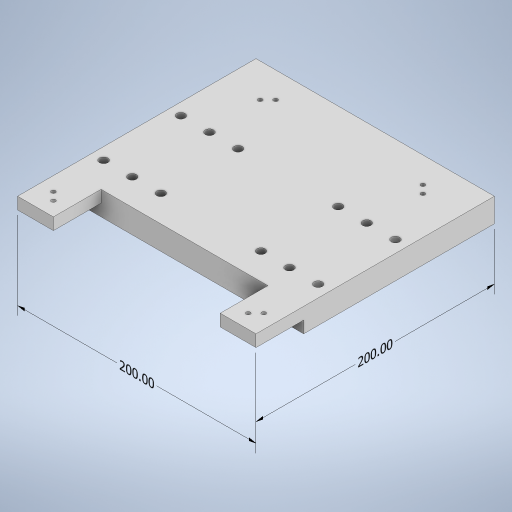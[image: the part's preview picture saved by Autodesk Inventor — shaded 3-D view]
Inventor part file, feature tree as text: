
AUTODESK INVENTOR PART (.ipt)
format: ipt  version: 2023 (Build 270158000, 158)  size: 317,952 bytes
history: native  units: mm
features: sketch x5, other x4, extrude x4, hole x1
ambient origin geometry x8: Origin, YZ Plane, XZ Plane, XY Plane, X Axis, Y Axis, Z Axis, Center Point
bodies: Body1 (feature_tree)
feature tree (14):
  other  "Sólido1"
  other  "Anotaciones"
  extrude  "Extrusión1"  Depth=160.0mm
  extrude  "Extrusión2"  TaperAngle=0.0deg  [1 undecoded]
  extrude  "Extrusión3"  Depth=20.0mm TaperAngle=0.0deg
  extrude  "Extrusión4"  Depth=10.0mm
  hole  "Agujero1"  [1 undecoded]
  sketch  "Boceto1"  dims[d0=200.0mm d1=160.0mm]
  sketch  "Boceto2"  dims[d2=20.0mm d3=0.0mm]
  sketch  "Boceto3"  dims[d4=7.0mm d5=68.0mm d6=80.0mm d7=7.6mm d8=10.0mm d9=7.0mm d10=24.0mm d11=10.0mm d16=0.0mm]
  sketch  "Boceto4"  dims[d19=40.0mm d20=20.0mm d21=0.0mm]
  sketch  "Boceto5"  dims[d22=30.0mm d23=10.0mm d24=40.0mm d25=0.0mm d26=1.75mm d27=8.25mm d28=20.0mm d29=10.0mm d30=10.0mm d31=1.75mm d32=1.75mm d33=1.75mm d34=40.0mm d35=0.0mm d36=11.749873mm d37=40.0mm d38=29.999873mm d39=21.75mm d40=11.75mm d41=28.300341mm d42=11.749873mm d43=0.0mm d44=0.0mm d45=3.5mm d46=6.0mm d47=4.0mm d48=2.0mm d49=90.0deg d50=8.0mm d51=20.594885mm d58=30.0mm d59=30.0mm d52=6.692993mm d53=5.009025mm d54=200.0mm d55=6.065637mm d56=3.288093mm d57=200.0mm]
  other  "Cota lineal 1"
  other  "Cota lineal 2"
note: 2 required parameter values undecoded (feature->parameter linkage not recoverable at this tier; creation-order binding heuristic only, values carry confidence <= 0.55)
